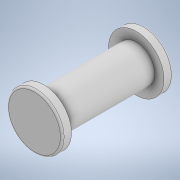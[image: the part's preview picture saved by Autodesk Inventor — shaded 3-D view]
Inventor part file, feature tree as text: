
AUTODESK INVENTOR PART (.ipt)
format: ipt  version: 2021 (Build 250183000, 183)  size: 128,000 bytes
history: native  units: in
note: dims shown in document units (in); Inventor stores cm internally (conversion verified against a paired STEP export)
features: extrude x3, sketch x3, plane x2, fillet x1
ambient origin geometry x8: Origin, YZ Plane, XZ Plane, XY Plane, X Axis, Y Axis, Z Axis, Center Point
bodies: Solid1 (feature_tree)
feature tree (9):
  extrude  "Extrusion1"  Depth=0.1969in TaperAngle=0.0deg
  plane  "Work Plane1"
  plane  "Work Plane2"
  extrude  "Extrusion2"  TaperAngle=0.0deg  [1 undecoded]
  extrude  "Extrusion3"  Depth=0.0197in TaperAngle=0.0deg
  fillet  "Fillet1"  Radius=0.1181in
  sketch  "Sketch1"  dims[d0=0.0787in d1=0.1969in d2=0.0in]
  sketch  "Sketch2"  dims[d3=0.0in d4=0.0in]
  sketch  "Sketch3"  dims[d5=0.1181in d6=0.0197in d7=0.0in d8=0.1181in d9=0.0197in d10=0.0in d11=0.0039in]
note: 1 required parameter value undecoded (feature->parameter linkage not recoverable at this tier; creation-order binding heuristic only, values carry confidence <= 0.55)
